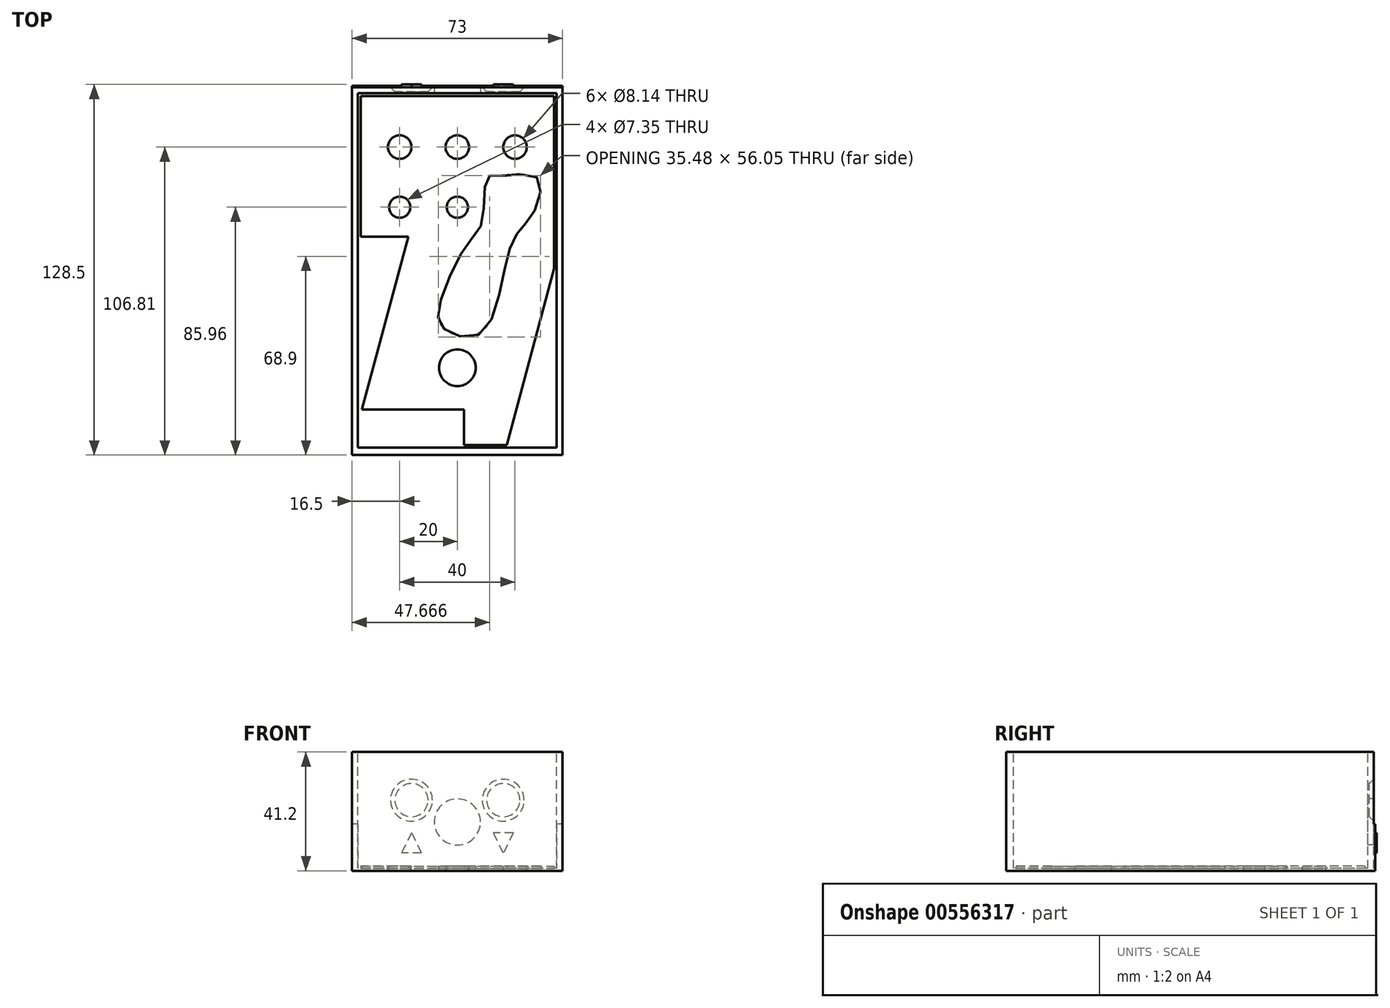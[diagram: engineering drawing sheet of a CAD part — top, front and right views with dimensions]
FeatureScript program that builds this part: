
annotation { "Feature Type Name" : "Feature", "Feature Type Description" : "" }
export const myFeature = defineFeature(function(context is Context, id is Id, definition is map)
    precondition{}
    {
        {
            var Q0;
            Q0=qCreatedBy(makeId("Top.planeOp"),FACE);
            var sketch = newSketch(context, id + "F0", { "sketchPlane" : qUnion([Q0])});
            skLineSegment(sketch, "E0.bottom", {"start": v(-36.5, 64) * mm, "end": v(36.5, 64) * mm});
            skLineSegment(sketch, "E0.top", {"start": v(-36.5, -64) * mm, "end": v(36.5, -64) * mm});
            skLineSegment(sketch, "E0.left", {"start": v(-36.5, 64) * mm, "end": v(-36.5, -64) * mm});
            skLineSegment(sketch, "E0.right", {"start": v(36.5, 64) * mm, "end": v(36.5, -64) * mm});
            skSolve(sketch);
        }
        {
            var Q0;
            Q0=makeQuery(id+"F0.imprint","IMPRINT",FACE,{"disambiguationData":[TD([[makeQuery(id+"F0.imprint","IMPRINT",EDGE,{"derivedFrom":sQuery(id+"F0.wireOp",EDGE,"E0.bottom")}),-1.0]])]});
            extrude(context, id + "F1", {"entities" : qUnion([Q0]), "depth" : 41.2 * mm, "offsetDistance" : 25 * mm});
        }
        {
            var Q0;
            Q0=makeQuery(id+"F1.opExtrude","SWEPT_FACE",FACE,{"disambiguationData":[OSD([sQuery(id+"F0.wireOp",EDGE,"E0.top")])]});
            var sketch = newSketch(context, id + "F2", { "sketchPlane" : qUnion([Q0])});
            skLineSegment(sketch, "E1.0", {"start": v(-36.5, 41.2) * mm, "end": v(-36.5, 0) * mm, "construction": true});
            skLineSegment(sketch, "E2", {"start": v(-36.5, 20.6) * mm, "end": v(36.5, 20.6) * mm, "construction": true});
            skLineSegment(sketch, "E3.bottom", {"start": v(-35.52, 54.74) * mm, "end": v(45.24, 40.5) * mm});
            skLineSegment(sketch, "E3.top", {"start": v(-45.07, 0.57) * mm, "end": v(35.68, -13.67) * mm});
            skLineSegment(sketch, "E3.left", {"start": v(-35.52, 54.74) * mm, "end": v(-45.07, 0.57) * mm});
            skLineSegment(sketch, "E3.right", {"start": v(45.24, 40.5) * mm, "end": v(35.68, -13.67) * mm});
            skPoint(sketch, "E3.middle", {"position": v(0, 20.6) * mm});
            skSolve(sketch);
        }
        {
            var Q0;
            Q0=makeQuery(id+"F1.opExtrude","SWEPT_FACE",FACE,{"disambiguationData":[OSD([sQuery(id+"F0.wireOp",EDGE,"E0.bottom")])]});
            var sketch = newSketch(context, id + "F3", { "sketchPlane" : qUnion([Q0])});
            skLineSegment(sketch, "E4.bottom", {"start": v(46.63, 40.44) * mm, "end": v(-37.08, 55.2) * mm});
            skLineSegment(sketch, "E4.top", {"start": v(37.08, -13.73) * mm, "end": v(-46.63, 1.03) * mm});
            skLineSegment(sketch, "E4.left", {"start": v(46.63, 40.44) * mm, "end": v(37.08, -13.73) * mm});
            skLineSegment(sketch, "E4.right", {"start": v(-37.08, 55.2) * mm, "end": v(-46.63, 1.03) * mm});
            skPoint(sketch, "E4.middle", {"position": v(0, 20.73) * mm});
            skSolve(sketch);
        }
        {
            var Q0;
            Q0=qCreatedBy(makeId("Top.planeOp"),FACE);
            cPlane(context, id + "F4", {"entities" : qUnion([Q0]), "cplaneType" : CPlaneType.OFFSET, "offset" : 41.2 * mm, "width" : 150 * mm, "height" : 150 * mm});
        }
        {
            var Q0;
            Q0=qCreatedBy(id+"F4.planeOp",FACE);
            var sketch = newSketch(context, id + "F5", { "sketchPlane" : qUnion([Q0])});
            skLineSegment(sketch, "E5.bottom", {"start": v(-34.5, 61.5) * mm, "end": v(34.5, 61.5) * mm});
            skLineSegment(sketch, "E5.top", {"start": v(-34.5, -61.5) * mm, "end": v(34.5, -61.5) * mm});
            skLineSegment(sketch, "E5.left", {"start": v(-34.5, 61.5) * mm, "end": v(-34.5, -61.5) * mm});
            skLineSegment(sketch, "E5.right", {"start": v(34.5, 61.5) * mm, "end": v(34.5, -61.5) * mm});
            skSolve(sketch);
        }
        {
            var Q0;
            Q0=makeQuery(id+"F5.imprint","IMPRINT",FACE,{"disambiguationData":[TD([[makeQuery(id+"F5.imprint","IMPRINT",EDGE,{"derivedFrom":sQuery(id+"F5.wireOp",EDGE,"E5.bottom")}),-1.0]])]});
            extrude(context, id + "F6", {"entities" : qUnion([Q0]), "operationType" : NewBodyOperationType.REMOVE, "oppositeDirection" : true, "depth" : 40.4 * mm, "offsetDistance" : 25 * mm, "hasSecondDirection" : true, "secondDirectionOppositeDirection" : false, "secondDirectionDepth" : 25 * mm});
        }
        {
            var Q0;
            Q0=makeQuery(id+"F6.boolean.opBoolean","COPY",FACE,{"derivedFrom":makeQuery(id+"F6.opExtrude","CAP_FACE",FACE,{"disambiguationData":[OSD([sQuery(id+"F5.wireOp",EDGE,"E5.bottom"),sQuery(id+"F5.wireOp",EDGE,"E5.top"),sQuery(id+"F5.wireOp",EDGE,"E5.left"),sQuery(id+"F5.wireOp",EDGE,"E5.right")])],"isStart":false})});
            var sketch = newSketch(context, id + "F7", { "sketchPlane" : qUnion([Q0])});
            skCircle(sketch, "E6", {"center": v(-20, 42.8) * mm, "radius": 4.07 * mm});
            skCircle(sketch, "E7", {"center": v(0, 42.8) * mm, "radius": 4.07 * mm});
            skCircle(sketch, "E8", {"center": v(20, 42.8) * mm, "radius": 4.07 * mm});
            skCircle(sketch, "E9", {"center": v(0, -33.73) * mm, "radius": 6.35 * mm});
            skLineSegment(sketch, "E10", {"start": v(20, 42.8) * mm, "end": v(0, 42.8) * mm, "construction": true});
            skCircle(sketch, "E11", {"center": v(0, 21.96) * mm, "radius": 3.67 * mm});
            skCircle(sketch, "E12", {"center": v(-20, 21.96) * mm, "radius": 3.67 * mm});
            skSolve(sketch);
        }
        {
            var Q0;
            Q0=qSketchRegion(id+"F7",true);
            extrude(context, id + "F8", {"entities" : qUnion([Q0]), "operationType" : NewBodyOperationType.REMOVE, "oppositeDirection" : true, "depth" : 25 * mm, "offsetDistance" : 25 * mm});
        }
        {
            var Q0;
            Q0=makeQuery(id+"F6.boolean.opBoolean","COPY",FACE,{"derivedFrom":makeQuery(id+"F6.opExtrude","SWEPT_FACE",FACE,{"disambiguationData":[OSD([sQuery(id+"F5.wireOp",EDGE,"E5.bottom")])]})});
            cPlane(context, id + "F9", {"entities" : qUnion([Q0]), "cplaneType" : CPlaneType.OFFSET, "offset" : 2 * mm, "oppositeDirection" : true, "width" : 150 * mm, "height" : 150 * mm});
        }
        {
            var Q0;
            Q0=qCreatedBy(id+"F9.planeOp",FACE);
            var sketch = newSketch(context, id + "F10", { "sketchPlane" : qUnion([Q0])});
            skCircle(sketch, "E13", {"center": v(0, 16.93) * mm, "radius": 8 * mm});
            skCircle(sketch, "E14", {"center": v(15.92, 24.5) * mm, "radius": 5.76 * mm});
            skCircle(sketch, "E15", {"center": v(-15.92, 24.5) * mm, "radius": 5.76 * mm});
            skSolve(sketch);
        }
        {
            var Q0;
            Q0=qSketchRegion(id+"F10",true);
            extrude(context, id + "F11", {"entities" : qUnion([Q0]), "operationType" : NewBodyOperationType.REMOVE, "endBound" : BoundingType.SYMMETRIC, "oppositeDirection" : true, "depth" : 30 * mm, "offsetDistance" : 25 * mm});
        }
        {
            var Q0;
            Q0=qCreatedBy(id+"F9.planeOp",FACE);
            var sketch = newSketch(context, id + "F12", { "sketchPlane" : qUnion([Q0])});
            skLineSegment(sketch, "E16.0", {"start": v(-34.5, 0.8) * mm, "end": v(-34.5, 43) * mm});
            skLineSegment(sketch, "E17.0", {"start": v(-34.5, 0.8) * mm, "end": v(34.5, 0.8) * mm});
            skLineSegment(sketch, "E18.0", {"start": v(34.5, 0.8) * mm, "end": v(34.5, 43) * mm});
            skLineSegment(sketch, "E19.0", {"start": v(-34.5, 43) * mm, "end": v(34.5, 43) * mm});
            skSolve(sketch);
        }
        {
            var Q0;
            Q0=qSketchRegion(id+"F12",true);
            extrude(context, id + "F13", {"entities" : qUnion([Q0]), "operationType" : NewBodyOperationType.REMOVE, "oppositeDirection" : true, "depth" : 25 * mm, "offsetDistance" : 25 * mm});
        }
        {
            var Q0;
            Q0=makeQuery(id+"F13.boolean.opBoolean","COPY",FACE,{"derivedFrom":makeQuery(id+"F13.opExtrude","CAP_FACE",FACE,{"disambiguationData":[OSD([sQuery(id+"F12.wireOp",EDGE,"E16.0"),sQuery(id+"F12.wireOp",EDGE,"E17.0"),sQuery(id+"F12.wireOp",EDGE,"E18.0"),sQuery(id+"F12.wireOp",EDGE,"E19.0")])],"isStart":true})});
            var sketch = newSketch(context, id + "F14", { "sketchPlane" : qUnion([Q0])});
            skLineSegment(sketch, "E20", {"start": v(75, 16.26) * mm, "end": v(-75, 16.26) * mm});
            skLineSegment(sketch, "E21", {"start": v(-75, 16.26) * mm, "end": v(-75, 44.5) * mm});
            skLineSegment(sketch, "E22", {"start": v(-75, 44.5) * mm, "end": v(75, 44.5) * mm});
            skLineSegment(sketch, "E23", {"start": v(75, 44.5) * mm, "end": v(75, 16.26) * mm});
            skSolve(sketch);
        }
        {
            var Q0;
            Q0=qSketchRegion(id+"F14",true);
            extrude(context, id + "F15", {"entities" : qUnion([Q0]), "operationType" : NewBodyOperationType.REMOVE, "depth" : 15 * mm, "offsetDistance" : 25 * mm});
        }
        {
            var Q0;
            Q0=makeQuery(id+"F13.boolean.opBoolean","INTERSECT",EDGE,{"derivedFrom":[makeQuery(id+"F11.boolean.opBoolean","COPY",FACE,{"derivedFrom":makeQuery(id+"F11.opExtrude","SWEPT_FACE",FACE,{"disambiguationData":[OSD([sQuery(id+"F10.wireOp",EDGE,"E15")])]})}),makeQuery(id+"F13.opExtrude","CAP_FACE",FACE,{"disambiguationData":[OSD([sQuery(id+"F12.wireOp",EDGE,"E16.0"),sQuery(id+"F12.wireOp",EDGE,"E17.0"),sQuery(id+"F12.wireOp",EDGE,"E18.0"),sQuery(id+"F12.wireOp",EDGE,"E19.0")])],"isStart":true})]});
            var Q1;
            Q1=makeQuery(id+"F13.boolean.opBoolean","INTERSECT",EDGE,{"derivedFrom":[makeQuery(id+"F11.boolean.opBoolean","COPY",FACE,{"derivedFrom":makeQuery(id+"F11.opExtrude","SWEPT_FACE",FACE,{"disambiguationData":[OSD([sQuery(id+"F10.wireOp",EDGE,"E14")])]})}),makeQuery(id+"F13.opExtrude","CAP_FACE",FACE,{"disambiguationData":[OSD([sQuery(id+"F12.wireOp",EDGE,"E16.0"),sQuery(id+"F12.wireOp",EDGE,"E17.0"),sQuery(id+"F12.wireOp",EDGE,"E18.0"),sQuery(id+"F12.wireOp",EDGE,"E19.0")])],"isStart":true})]});
            chamfer(context, id + "F16", {"entities" : qUnion([Q0, Q1]), "width" : 1.5 * mm, "tangentPropagation" : true});
        }
        {
            var Q0;
            Q0=makeQuery(id+"F15.boolean.opBoolean","MERGE",FACE,{"derivedFrom":[makeQuery(id+"F13.boolean.opBoolean","COPY",FACE,{"derivedFrom":makeQuery(id+"F13.opExtrude","CAP_FACE",FACE,{"disambiguationData":[OSD([sQuery(id+"F12.wireOp",EDGE,"E16.0"),sQuery(id+"F12.wireOp",EDGE,"E17.0"),sQuery(id+"F12.wireOp",EDGE,"E18.0"),sQuery(id+"F12.wireOp",EDGE,"E19.0")])],"isStart":true})}),makeQuery(id+"F15.opExtrude","CAP_FACE",FACE,{"disambiguationData":[OSD([sQuery(id+"F14.wireOp",EDGE,"E20"),sQuery(id+"F14.wireOp",EDGE,"E21"),sQuery(id+"F14.wireOp",EDGE,"E22"),sQuery(id+"F14.wireOp",EDGE,"E23")])],"isStart":true})]});
            var sketch = newSketch(context, id + "F17", { "sketchPlane" : qUnion([Q0])});
            skLineSegment(sketch, "E24", {"start": v(15.92, 24.5) * mm, "end": v(15.92, 6.07) * mm, "construction": true});
            skLineSegment(sketch, "E25", {"start": v(-15.92, 24.5) * mm, "end": v(-15.92, 6.07) * mm, "construction": true});
            skLineSegment(sketch, "E26", {"start": v(-19.42, 13.12) * mm, "end": v(-15.92, 13.12) * mm});
            skLineSegment(sketch, "E27", {"start": v(-19.42, 13.12) * mm, "end": v(-15.92, 6.12) * mm});
            skLineSegment(sketch, "E28", {"start": v(15.92, 13.12) * mm, "end": v(19.42, 6.12) * mm});
            skLineSegment(sketch, "E29", {"start": v(19.42, 6.12) * mm, "end": v(15.92, 6.12) * mm});
            skLineSegment(sketch, "E30.MirrorCS", {"start": v(12.42, 6.12) * mm, "end": v(15.92, 6.12) * mm});
            skLineSegment(sketch, "E31.MirrorCS", {"start": v(15.92, 13.12) * mm, "end": v(12.42, 6.12) * mm});
            skLineSegment(sketch, "E32.MirrorCS", {"start": v(-12.42, 13.12) * mm, "end": v(-15.92, 6.12) * mm});
            skLineSegment(sketch, "E33.MirrorCS", {"start": v(-12.42, 13.12) * mm, "end": v(-15.92, 13.12) * mm});
            skSolve(sketch);
        }
        {
            var Q0;
            Q0=qSketchRegion(id+"F17",true);
            extrude(context, id + "F18", {"entities" : qUnion([Q0]), "operationType" : NewBodyOperationType.ADD, "depth" : 1 * mm, "offsetDistance" : 25 * mm});
        }
        {
            var Q0;
            {var subQ0=sQuery(id+"F5.wireOp",EDGE,"E5.bottom");var subQ1=sQuery(id+"F5.wireOp",EDGE,"E5.left");var subQ2=sQuery(id+"F5.wireOp",EDGE,"E5.top");var subQ3=sQuery(id+"F5.wireOp",EDGE,"E5.right");Q0=makeQuery(id+"FWr3AL7p3hajMNo_1.boolean.opBoolean","SPLIT",FACE,{"disambiguationData":[TD([makeQuery(id+"F6.boolean.opBoolean","COPY",FACE,{"derivedFrom":makeQuery(id+"F6.opExtrude","SWEPT_FACE",FACE,{"disambiguationData":[OSD([subQ0])]})})])],"derivedFrom":makeQuery(id+"F6.boolean.opBoolean","COPY",FACE,{"derivedFrom":makeQuery(id+"F6.opExtrude","CAP_FACE",FACE,{"disambiguationData":[OSD([subQ0,subQ2,subQ1,subQ3])],"isStart":false})})});}
            var sketch = newSketch(context, id + "F19", { "sketchPlane" : qUnion([Q0])});
            skLineSegment(sketch, "E34.bottom", {"start": v(-33.5, 60.5) * mm, "end": v(33.5, 60.5) * mm});
            skLineSegment(sketch, "E34.top", {"start": v(2.3, -60.5) * mm, "end": v(17.13, -60.5) * mm});
            skLineSegment(sketch, "E34.left", {"start": v(-33.5, 60.5) * mm, "end": v(-33.5, 11.66) * mm});
            skLineSegment(sketch, "E34.right", {"start": v(33.5, 60.5) * mm, "end": v(33.5, 0.6) * mm});
            skPoint(sketch, "E34.middle", {"position": v(0, 0) * mm});
            skCircle(sketch, "E35.0", {"center": v(-20, 42.8) * mm, "radius": 4.07 * mm});
            skCircle(sketch, "E36.0", {"center": v(0, 42.8) * mm, "radius": 4.07 * mm});
            skCircle(sketch, "E37.0", {"center": v(20, 42.8) * mm, "radius": 4.07 * mm});
            skCircle(sketch, "E38.0", {"center": v(0, 21.96) * mm, "radius": 3.67 * mm});
            skCircle(sketch, "E39.0", {"center": v(-20, 21.96) * mm, "radius": 3.68 * mm});
            skCircle(sketch, "E40.0", {"center": v(0, -33.73) * mm, "radius": 6.35 * mm});
            skFitSpline(sketch, "E41", {"points": [v(15.6, 32.92) * mm, v(10.24, 32.07) * mm, v(8.74, 17.26) * mm, v(3.16, 8.67) * mm, v(-6.28, -12.57) * mm, v(-4.57, -20.3) * mm, v(7.88, -22.02) * mm, v(16.25, 0) * mm, v(20.97, 13.18) * mm, v(26.55, 20.26) * mm, v(27.84, 32.07) * mm, v(15.6, 32.92) * mm]});
            skLineSegment(sketch, "E42", {"start": v(-33.1, -48.2) * mm, "end": v(-17.05, 11.66) * mm});
            skLineSegment(sketch, "E43", {"start": v(-17.05, 11.66) * mm, "end": v(-33.5, 11.66) * mm});
            skLineSegment(sketch, "E44", {"start": v(-33.1, -48.2) * mm, "end": v(2.3, -48.2) * mm});
            skLineSegment(sketch, "E45", {"start": v(2.3, -48.2) * mm, "end": v(2.3, -60.5) * mm});
            skPoint(sketch, "E46.orphan", {"position": v(-33.5, -60.5) * mm});
            skLineSegment(sketch, "E47", {"start": v(17.13, -60.5) * mm, "end": v(33.5, 0.6) * mm});
            skPoint(sketch, "E48.orphan", {"position": v(33.5, -60.5) * mm});
            skSolve(sketch);
        }
        {
            var Q0;
            Q0=qSketchRegion(id+"F19",true);
            extrude(context, id + "F20", {"entities" : qUnion([Q0]), "depth" : 0.8 * mm, "offsetDistance" : 25 * mm});
        }
        {
            var Q0;
            Q0=qCreatedBy(makeId("Top.planeOp"),FACE);
            var sketch = newSketch(context, id + "F21", { "sketchPlane" : qUnion([Q0])});
            skCircle(sketch, "E49.0", {"center": v(0, -33.73) * mm, "radius": 6.35 * mm, "construction": true});
            skCircle(sketch, "E50.0", {"center": v(0, 21.96) * mm, "radius": 3.67 * mm, "construction": true});
            skCircle(sketch, "E51.0", {"center": v(20, 42.8) * mm, "radius": 4.07 * mm, "construction": true});
            skCircle(sketch, "E52.0", {"center": v(0, 42.8) * mm, "radius": 4.07 * mm, "construction": true});
            skCircle(sketch, "E53.0", {"center": v(-20, 21.96) * mm, "radius": 3.68 * mm, "construction": true});
            skCircle(sketch, "E54.0", {"center": v(-20, 42.8) * mm, "radius": 4.07 * mm, "construction": true});
            skCircle(sketch, "E55", {"center": v(0, -33.73) * mm, "radius": 9.35 * mm});
            skCircle(sketch, "E56", {"center": v(0, 21.96) * mm, "radius": 6.68 * mm});
            skCircle(sketch, "E57", {"center": v(20, 42.8) * mm, "radius": 9.07 * mm});
            skCircle(sketch, "E58", {"center": v(0, 42.8) * mm, "radius": 9.07 * mm});
            skCircle(sketch, "E59", {"center": v(-20, 21.96) * mm, "radius": 6.68 * mm});
            skCircle(sketch, "E60", {"center": v(-20, 42.8) * mm, "radius": 9.07 * mm});
            skSolve(sketch);
        }
        {
            var Q0;
            Q0=qCreatedBy(id+"F4.planeOp",FACE);
            var sketch = newSketch(context, id + "F22", { "sketchPlane" : qUnion([Q0])});
            skLineSegment(sketch, "E61.bottom", {"start": v(61.89, -73.5) * mm, "end": v(-61.89, -73.5) * mm});
            skLineSegment(sketch, "E61.top", {"start": v(61.89, 73.5) * mm, "end": v(-61.89, 73.5) * mm});
            skLineSegment(sketch, "E61.left", {"start": v(61.89, -73.5) * mm, "end": v(61.89, 73.5) * mm});
            skLineSegment(sketch, "E61.right", {"start": v(-61.89, -73.5) * mm, "end": v(-61.89, 73.5) * mm});
            skPoint(sketch, "E61.middle", {"position": v(0, 0) * mm});
            skSolve(sketch);
        }
        {
            var Q0;
            Q0 = qSketchRegion(id + "F22", true);
            extrude(context, id + "F23", {"entities" : qUnion([Q0]), "operationType" : NewBodyOperationType.REMOVE, "depth" : 25 * mm, "offsetDistance" : 25 * mm});
        }
    });
